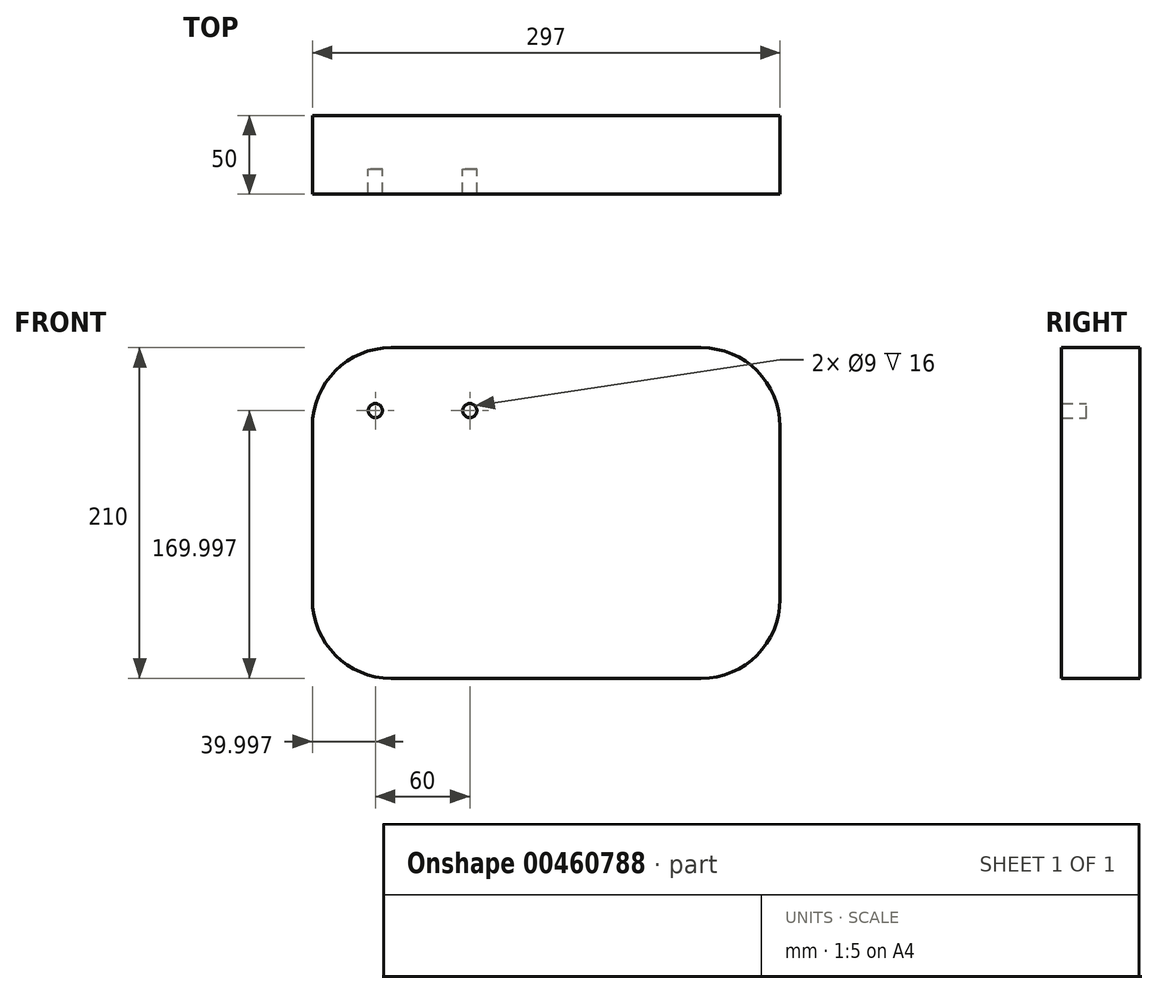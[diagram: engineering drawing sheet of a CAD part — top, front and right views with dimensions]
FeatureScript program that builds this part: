
annotation { "Feature Type Name" : "Feature", "Feature Type Description" : "" }
export const myFeature = defineFeature(function(context is Context, id is Id, definition is map)
    precondition{}
    {
        {
            var Q0;
            Q0=qCreatedBy(makeId("Front.planeOp"),FACE);
            var sketch = newSketch(context, id + "F0", { "sketchPlane" : qUnion([Q0])});
            skLineSegment(sketch, "E0.bottom", {"start": v(-107.95, 101.75) * mm, "end": v(89.05, 101.75) * mm});
            skLineSegment(sketch, "E0.top", {"start": v(-107.95, -108.25) * mm, "end": v(89.05, -108.25) * mm});
            skLineSegment(sketch, "E0.left", {"start": v(-157.95, 51.75) * mm, "end": v(-157.95, -58.25) * mm});
            skLineSegment(sketch, "E0.right", {"start": v(139.05, 51.75) * mm, "end": v(139.05, -58.25) * mm});
            skPoint(sketch, "E1.visualSharp", {"position": v(-157.95, 101.75) * mm});
            skArc(sketch, "E1.filletArc", {"start": v(-107.95, 101.75) * mm, "mid": v(-143.3, 87.1) * mm, "end": v(-157.95, 51.75) * mm});
            skPoint(sketch, "E2.visualSharp", {"position": v(139.05, 101.75) * mm});
            skArc(sketch, "E2.filletArc", {"start": v(139.05, 51.75) * mm, "mid": v(124.4, 87.1) * mm, "end": v(89.05, 101.75) * mm});
            skPoint(sketch, "E3.visualSharp", {"position": v(-157.95, -108.25) * mm});
            skArc(sketch, "E3.filletArc", {"start": v(-157.95, -58.25) * mm, "mid": v(-143.3, -93.6) * mm, "end": v(-107.95, -108.25) * mm});
            skPoint(sketch, "E4.visualSharp", {"position": v(139.05, -108.25) * mm});
            skArc(sketch, "E4.filletArc", {"start": v(89.05, -108.25) * mm, "mid": v(124.4, -93.6) * mm, "end": v(139.05, -58.25) * mm});
            skSolve(sketch);
        }
        {
            var Q0;
            Q0=makeQuery(id+"F0.imprint","IMPRINT",FACE,{"disambiguationData":[TD([[makeQuery(id+"F0.imprint","IMPRINT",EDGE,{"derivedFrom":sQuery(id+"F0.wireOp",EDGE,"E0.bottom")}),-1.0]])]});
            var sketch = newSketch(context, id + "F1", { "sketchPlane" : qUnion([Q0])});
            skSolve(sketch);
        }
        {
            var Q0;
            Q0=makeQuery(id+"F0.imprint","IMPRINT",FACE,{"disambiguationData":[TD([[makeQuery(id+"F0.imprint","IMPRINT",EDGE,{"derivedFrom":sQuery(id+"F0.wireOp",EDGE,"E0.bottom")}),-1.0]])]});
            extrude(context, id + "F2", {"entities" : qUnion([Q0]), "depth" : 9 * mm});
        }
        {
            var Q0;
            Q0=makeQuery(id+"F2.opExtrude","CAP_FACE",FACE,{"disambiguationData":[OSD([sQuery(id+"F0.wireOp",EDGE,"E0.bottom"),sQuery(id+"F0.wireOp",EDGE,"E0.top"),sQuery(id+"F0.wireOp",EDGE,"E0.left"),sQuery(id+"F0.wireOp",EDGE,"E0.right"),sQuery(id+"F0.wireOp",EDGE,"E1.filletArc"),sQuery(id+"F0.wireOp",EDGE,"E2.filletArc"),sQuery(id+"F0.wireOp",EDGE,"E3.filletArc"),sQuery(id+"F0.wireOp",EDGE,"E4.filletArc")])],"isStart":false});
            var sketch = newSketch(context, id + "F3", { "sketchPlane" : qUnion([Q0])});
            skCircle(sketch, "E5", {"center": v(-117.95, 61.75) * mm, "radius": 4.5 * mm});
            skCircle(sketch, "E6", {"center": v(-57.95, 61.75) * mm, "radius": 4.5 * mm});
            skSolve(sketch);
        }
        {
            var Q0;
            Q0=makeQuery(id+"F3.imprint","IMPRINT",FACE,{"disambiguationData":[TD([[makeQuery(id+"F3.imprint","IMPRINT",EDGE,{"derivedFrom":sQuery(id+"F3.wireOp",EDGE,"E5")}),1.0]])]});
            var Q1;
            Q1=makeQuery(id+"F3.imprint","IMPRINT",FACE,{"disambiguationData":[TD([[makeQuery(id+"F3.imprint","IMPRINT",EDGE,{"derivedFrom":sQuery(id+"F3.wireOp",EDGE,"E6")}),1.0]])]});
            extrude(context, id + "F4", {"entities" : qUnion([Q0, Q1]), "operationType" : NewBodyOperationType.ADD, "depth" : 25 * mm});
        }
        {
            var Q0;
            Q0=makeQuery(id+"F2.opExtrude","CAP_FACE",FACE,{"disambiguationData":[OSD([sQuery(id+"F0.wireOp",EDGE,"E0.bottom"),sQuery(id+"F0.wireOp",EDGE,"E0.top"),sQuery(id+"F0.wireOp",EDGE,"E0.left"),sQuery(id+"F0.wireOp",EDGE,"E0.right"),sQuery(id+"F0.wireOp",EDGE,"E1.filletArc"),sQuery(id+"F0.wireOp",EDGE,"E2.filletArc"),sQuery(id+"F0.wireOp",EDGE,"E3.filletArc"),sQuery(id+"F0.wireOp",EDGE,"E4.filletArc")])],"isStart":false});
            var sketch = newSketch(context, id + "F5", { "sketchPlane" : qUnion([Q0])});
            skLineSegment(sketch, "E7.bottom", {"start": v(61.56, 56.98) * mm, "end": v(179.24, 56.98) * mm});
            skLineSegment(sketch, "E7.top", {"start": v(61.56, 26.18) * mm, "end": v(179.24, 26.18) * mm});
            skLineSegment(sketch, "E7.left", {"start": v(61.56, 56.98) * mm, "end": v(61.56, 26.18) * mm});
            skLineSegment(sketch, "E7.right", {"start": v(179.24, 56.98) * mm, "end": v(179.24, 26.18) * mm});
            skSolve(sketch);
        }
        {
            var Q0;
            {var subQ0=sQuery(id+"F5.wireOp",EDGE,"E7.left");Q0=makeQuery(id+"F5.imprint","IMPRINT",FACE,{"disambiguationData":[TD([[makeQuery(id+"F5.imprint","IMPRINT",EDGE,{"derivedFrom":subQ0}),1.0]])]});}
            extrude(context, id + "F6", {"entities" : qUnion([Q0]), "operationType" : NewBodyOperationType.REMOVE, "oppositeDirection" : true, "depth" : 25 * mm});
        }
        {
            var Q0;
            Q0=makeQuery(id+"F1.imprint","IMPRINT",FACE,{"disambiguationData":[TD([[makeQuery(id+"F1.imprint","IMPRINT",EDGE,{"derivedFrom":makeQuery(id+"F0.imprint","IMPRINT",EDGE,{"derivedFrom":sQuery(id+"F0.wireOp",EDGE,"E0.bottom")})}),-1.0]])]});
            extrude(context, id + "F7", {"entities" : qUnion([Q0]), "operationType" : NewBodyOperationType.ADD, "depth" : 25 * mm});
        }
        {
            var Q0;
            Q0=makeQuery(id+"F7.opExtrude","CAP_FACE",FACE,{"disambiguationData":[OSD([sQuery(id+"F0.wireOp",EDGE,"E0.bottom"),sQuery(id+"F0.wireOp",EDGE,"E0.top"),sQuery(id+"F0.wireOp",EDGE,"E0.left"),sQuery(id+"F0.wireOp",EDGE,"E0.right"),sQuery(id+"F0.wireOp",EDGE,"E1.filletArc"),sQuery(id+"F0.wireOp",EDGE,"E2.filletArc"),sQuery(id+"F0.wireOp",EDGE,"E3.filletArc"),sQuery(id+"F0.wireOp",EDGE,"E4.filletArc")])],"isStart":false});
            var sketch = newSketch(context, id + "F8", { "sketchPlane" : qUnion([Q0])});
            skSolve(sketch);
        }
        {
            var Q0;
            {var subQ3=sQuery(id+"F0.wireOp",EDGE,"E0.bottom");Q0=makeQuery(id+"F8.imprint","IMPRINT",FACE,{"disambiguationData":[TD([[makeQuery(id+"F8.imprint","IMPRINT",EDGE,{"derivedFrom":makeQuery(id+"F7.opExtrude","CAP_EDGE",EDGE,{"disambiguationData":[OSD([subQ3])],"isStart":false})}),-1.0]])]});}
            extrude(context, id + "F9", {"entities" : qUnion([Q0]), "operationType" : NewBodyOperationType.ADD, "depth" : 25 * mm});
        }
    });
